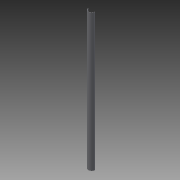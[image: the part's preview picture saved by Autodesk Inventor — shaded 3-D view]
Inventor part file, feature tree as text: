
AUTODESK INVENTOR PART (.ipt)
format: ipt  version: 2015 SP1 (Build 190203100, 203)  size: 84,480 bytes
history: native  units: mm
features: other x3, sketch x2
ambient origin geometry x8: Origin, YZ Plane, XZ Plane, XY Plane, X Axis, Y Axis, Z Axis, Center Point
bodies: Solid1 (feature_tree)
feature tree (5):
  other  "Tube sous miroir.ipt"
  other  "Solid1::Tube sous miroir.ipt"
  other  "TaggingFeature1"
  sketch  "Sketch1"  dims[d0=10.0mm]
  sketch  "Sketch2"
